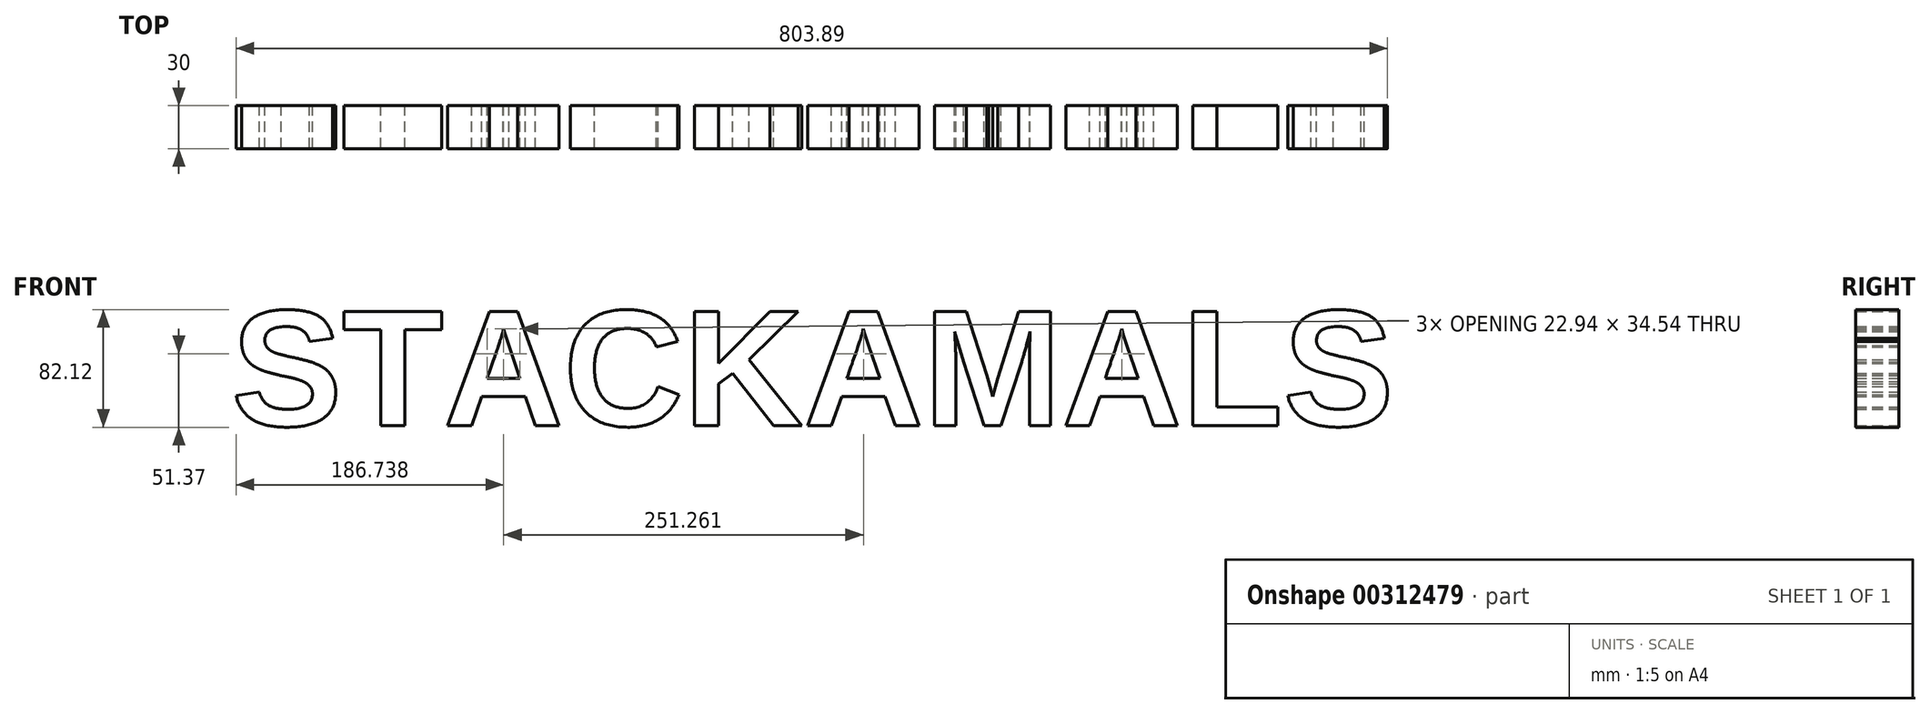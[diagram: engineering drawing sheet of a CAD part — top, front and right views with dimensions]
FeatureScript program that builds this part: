
annotation { "Feature Type Name" : "Feature", "Feature Type Description" : "" }
export const myFeature = defineFeature(function(context is Context, id is Id, definition is map)
    precondition{}
    {
        {
            var Q0;
            Q0=qCreatedBy(makeId("Front.planeOp"),FACE);
            var sketch = newSketch(context, id + "F0", { "sketchPlane" : qUnion([Q0])});
            skText(sketch, "E0", { "text": "STACKAMALS", "fontName": "Arimo-Bold.ttf"});
            const initialGuessF0  = {"E0": [-0.81529, 0, 1, 0, 0.0835]};
            skSetInitialGuess(sketch, initialGuessF0);
            skSolve(sketch);
        }
        {
            var Q0;
            Q0=makeQuery(id+"F0.imprint","IMPRINT",FACE,{"disambiguationData":[TD([[makeQuery(id+"F0.imprint","IMPRINT",EDGE,{"derivedFrom":sQuery(id+"F0.wireOp",EDGE,"E0.sketch_text.stroke-0")}),-1.0]])]});
            var Q1;
            Q1=makeQuery(id+"F0.imprint","IMPRINT",FACE,{"disambiguationData":[TD([[makeQuery(id+"F0.imprint","IMPRINT",EDGE,{"derivedFrom":sQuery(id+"F0.wireOp",EDGE,"E0.sketch_text.stroke-31")}),-1.0]])]});
            var Q2;
            Q2=makeQuery(id+"F0.imprint","IMPRINT",FACE,{"disambiguationData":[TD([[makeQuery(id+"F0.imprint","IMPRINT",EDGE,{"derivedFrom":sQuery(id+"F0.wireOp",EDGE,"E0.sketch_text.stroke-39")}),-1.0]])]});
            var Q3;
            Q3=makeQuery(id+"F0.imprint","IMPRINT",FACE,{"disambiguationData":[TD([[makeQuery(id+"F0.imprint","IMPRINT",EDGE,{"derivedFrom":sQuery(id+"F0.wireOp",EDGE,"E0.sketch_text.stroke-54")}),-1.0]])]});
            var Q4;
            Q4=makeQuery(id+"F0.imprint","IMPRINT",FACE,{"disambiguationData":[TD([[makeQuery(id+"F0.imprint","IMPRINT",EDGE,{"derivedFrom":sQuery(id+"F0.wireOp",EDGE,"E0.sketch_text.stroke-71")}),-1.0]])]});
            var Q5;
            Q5=makeQuery(id+"F0.imprint","IMPRINT",FACE,{"disambiguationData":[TD([[makeQuery(id+"F0.imprint","IMPRINT",EDGE,{"derivedFrom":sQuery(id+"F0.wireOp",EDGE,"E0.sketch_text.stroke-83")}),-1.0]])]});
            var Q6;
            Q6=makeQuery(id+"F0.imprint","IMPRINT",FACE,{"disambiguationData":[TD([[makeQuery(id+"F0.imprint","IMPRINT",EDGE,{"derivedFrom":sQuery(id+"F0.wireOp",EDGE,"E0.sketch_text.stroke-98")}),-1.0]])]});
            var Q7;
            Q7=makeQuery(id+"F0.imprint","IMPRINT",FACE,{"disambiguationData":[TD([[makeQuery(id+"F0.imprint","IMPRINT",EDGE,{"derivedFrom":sQuery(id+"F0.wireOp",EDGE,"E0.sketch_text.stroke-119")}),-1.0]])]});
            var Q8;
            Q8=makeQuery(id+"F0.imprint","IMPRINT",FACE,{"disambiguationData":[TD([[makeQuery(id+"F0.imprint","IMPRINT",EDGE,{"derivedFrom":sQuery(id+"F0.wireOp",EDGE,"E0.sketch_text.stroke-134")}),-1.0]])]});
            var Q9;
            Q9=makeQuery(id+"F0.imprint","IMPRINT",FACE,{"disambiguationData":[TD([[makeQuery(id+"F0.imprint","IMPRINT",EDGE,{"derivedFrom":sQuery(id+"F0.wireOp",EDGE,"E0.sketch_text.stroke-140")}),-1.0]])]});
            extrude(context, id + "F1", {"entities" : qUnion([Q0, Q1, Q2, Q3, Q4, Q5, Q6, Q7, Q8, Q9]), "depth" : 30 * mm, "offsetDistance" : 25 * mm});
        }
    });
